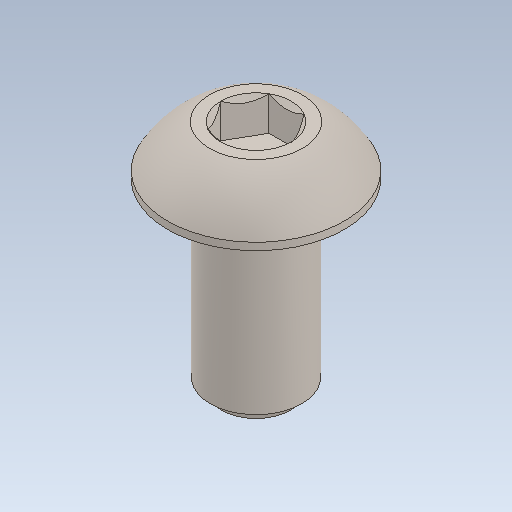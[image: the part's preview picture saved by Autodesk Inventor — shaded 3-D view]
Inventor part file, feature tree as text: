
AUTODESK INVENTOR PART (.ipt)
format: ipt  version: 2020 (Build 240168000, 168)  size: 134,656 bytes
history: native  units: in
note: dims shown in document units (in); Inventor stores cm internally (conversion verified against a paired STEP export)
features: fillet x1
ambient origin geometry x8: Origin, YZ Plane, XZ Plane, XY Plane, X Axis, Y Axis, Z Axis, Center Point
bodies: Solid1 (feature_tree)
feature tree (1):
  fillet  "Fillet1"  [1 undecoded]
note: 1 required parameter value undecoded (feature->parameter linkage not recoverable at this tier; creation-order binding heuristic only, values carry confidence <= 0.55)
